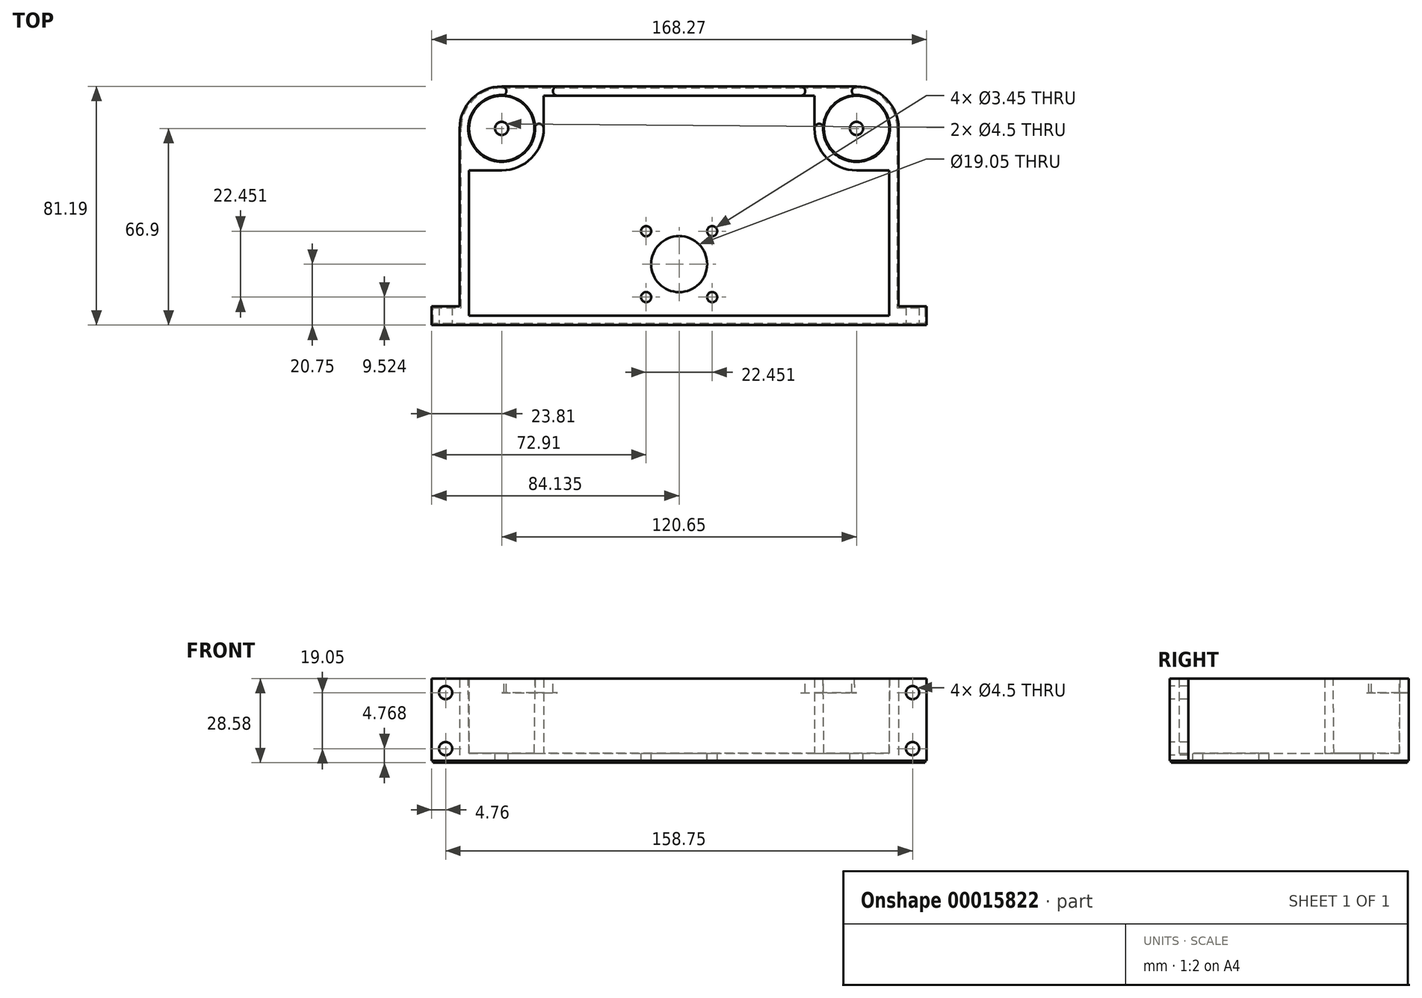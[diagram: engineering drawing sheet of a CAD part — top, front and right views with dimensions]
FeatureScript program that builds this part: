
annotation { "Feature Type Name" : "Feature", "Feature Type Description" : "" }
export const myFeature = defineFeature(function(context is Context, id is Id, definition is map)
    precondition{}
    {
        {
            var Q0;
            Q0=qCreatedBy(makeId("Top.planeOp"),FACE);
            var sketch = newSketch(context, id + "F0", { "sketchPlane" : qUnion([Q0])});
            skCircle(sketch, "E0", {"center": v(0, 0) * mm, "radius": 11.11 * mm});
            skLineSegment(sketch, "E1", {"start": v(0, 0) * mm, "end": v(120.65, 0) * mm, "construction": true});
            skCircle(sketch, "E2", {"center": v(120.65, 0) * mm, "radius": 11.11 * mm});
            skArc(sketch, "E3", {"start": v(0, 14.29) * mm, "mid": v(-10.1, 10.1) * mm, "end": v(-14.29, 0) * mm});
            skArc(sketch, "E4", {"start": v(134.94, 0) * mm, "mid": v(130.75, 10.1) * mm, "end": v(120.65, 14.29) * mm});
            skLineSegment(sketch, "E5", {"start": v(-14.29, 0) * mm, "end": v(-14.29, -60.55) * mm});
            skLineSegment(sketch, "E6", {"start": v(134.94, 0) * mm, "end": v(134.94, -60.55) * mm});
            skLineSegment(sketch, "E7", {"start": v(134.94, -60.55) * mm, "end": v(144.46, -60.55) * mm});
            skLineSegment(sketch, "E8", {"start": v(144.46, -60.55) * mm, "end": v(144.46, -66.9) * mm});
            skLineSegment(sketch, "E9", {"start": v(144.46, -66.9) * mm, "end": v(-23.81, -66.9) * mm});
            skLineSegment(sketch, "E10", {"start": v(-23.81, -66.9) * mm, "end": v(-23.81, -60.55) * mm});
            skLineSegment(sketch, "E11", {"start": v(-23.81, -60.55) * mm, "end": v(-14.29, -60.55) * mm});
            skLineSegment(sketch, "E12", {"start": v(0, 14.29) * mm, "end": v(120.65, 14.29) * mm});
            skLineSegment(sketch, "E13", {"start": v(60.33, 0) * mm, "end": v(60.33, -66.9) * mm, "construction": true});
            skSolve(sketch);
        }
        {
            var Q0;
            Q0=qSketchRegion(id+"F0",true);
            extrude(context, id + "F1", {"entities" : qUnion([Q0]), "depth" : 25.4 * mm});
        }
        {
            var Q0;
            Q0=makeQuery(id+"F1.opExtrude","CAP_FACE",FACE,{"disambiguationData":[OSD([sQuery(id+"F0.wireOp",EDGE,"E0"),sQuery(id+"F0.wireOp",EDGE,"E2"),sQuery(id+"F0.wireOp",EDGE,"vQT7KybJ-lzgk-kh55-kQ7M-RuszsokMCCUL"),sQuery(id+"F0.wireOp",EDGE,"E3"),sQuery(id+"F0.wireOp",EDGE,"E4"),sQuery(id+"F0.wireOp",EDGE,"E5"),sQuery(id+"F0.wireOp",EDGE,"E6"),sQuery(id+"F0.wireOp",EDGE,"E7"),sQuery(id+"F0.wireOp",EDGE,"E8"),sQuery(id+"F0.wireOp",EDGE,"E9"),sQuery(id+"F0.wireOp",EDGE,"E10"),sQuery(id+"F0.wireOp",EDGE,"E11")])],"isStart":false});
            shell(context, id + "F2", {"entities" : qUnion([Q0]), "thickness" : 3.17 * mm});
        }
        {
            var Q0;
            Q0=makeQuery(id+"F2.opShell","OFFSET_FACE",FACE,{"disambiguationData":[OSD([sQuery(id+"F0.wireOp",EDGE,"E0"),sQuery(id+"F0.wireOp",EDGE,"E2"),sQuery(id+"F0.wireOp",EDGE,"vQT7KybJ-lzgk-kh55-kQ7M-RuszsokMCCUL"),sQuery(id+"F0.wireOp",EDGE,"E3"),sQuery(id+"F0.wireOp",EDGE,"E4"),sQuery(id+"F0.wireOp",EDGE,"E5"),sQuery(id+"F0.wireOp",EDGE,"E6"),sQuery(id+"F0.wireOp",EDGE,"E7"),sQuery(id+"F0.wireOp",EDGE,"E8"),sQuery(id+"F0.wireOp",EDGE,"E9"),sQuery(id+"F0.wireOp",EDGE,"E10"),sQuery(id+"F0.wireOp",EDGE,"E11")])]});
            var sketch = newSketch(context, id + "F3", { "sketchPlane" : qUnion([Q0])});
            skArc(sketch, "E14", {"start": v(14.29, 0) * mm, "mid": v(12.9, 6.16) * mm, "end": v(8.98, 11.11) * mm});
            skArc(sketch, "E15", {"start": v(-11.11, -8.98) * mm, "mid": v(-6.16, -12.9) * mm, "end": v(0, -14.29) * mm});
            skLineSegment(sketch, "E16.bottom", {"start": v(-11.11, -8.98) * mm, "end": v(0, -8.98) * mm, "construction": true});
            skLineSegment(sketch, "E16.top", {"start": v(-11.11, -14.29) * mm, "end": v(0, -14.29) * mm});
            skLineSegment(sketch, "E16.left", {"start": v(-11.11, -8.98) * mm, "end": v(-11.11, -14.29) * mm});
            skLineSegment(sketch, "E16.right", {"start": v(0, -8.98) * mm, "end": v(0, -14.29) * mm, "construction": true});
            skLineSegment(sketch, "E17.bottom", {"start": v(14.29, 0) * mm, "end": v(8.98, 0) * mm, "construction": true});
            skLineSegment(sketch, "E17.top", {"start": v(14.29, 11.11) * mm, "end": v(8.98, 11.11) * mm});
            skLineSegment(sketch, "E17.left", {"start": v(14.29, 0) * mm, "end": v(14.29, 11.11) * mm});
            skLineSegment(sketch, "E17.right", {"start": v(8.98, 0) * mm, "end": v(8.98, 11.11) * mm, "construction": true});
            skArc(sketch, "E18", {"start": v(111.67, 11.11) * mm, "mid": v(107.76, 6.16) * mm, "end": v(106.36, 0) * mm});
            skArc(sketch, "E19", {"start": v(120.65, -14.29) * mm, "mid": v(126.8, -12.9) * mm, "end": v(131.76, -8.98) * mm});
            skLineSegment(sketch, "E20.bottom", {"start": v(106.36, 0) * mm, "end": v(111.67, 0) * mm, "construction": true});
            skLineSegment(sketch, "E20.top", {"start": v(106.36, 11.11) * mm, "end": v(111.67, 11.11) * mm});
            skLineSegment(sketch, "E20.left", {"start": v(106.36, 0) * mm, "end": v(106.36, 11.11) * mm});
            skLineSegment(sketch, "E20.right", {"start": v(111.67, 0) * mm, "end": v(111.67, 11.11) * mm, "construction": true});
            skLineSegment(sketch, "E21.bottom", {"start": v(120.65, -14.29) * mm, "end": v(131.76, -14.29) * mm});
            skLineSegment(sketch, "E21.top", {"start": v(120.65, -8.98) * mm, "end": v(131.76, -8.98) * mm, "construction": true});
            skLineSegment(sketch, "E21.left", {"start": v(120.65, -14.29) * mm, "end": v(120.65, -8.98) * mm, "construction": true});
            skLineSegment(sketch, "E21.right", {"start": v(131.76, -14.29) * mm, "end": v(131.76, -8.98) * mm});
            skSolve(sketch);
        }
        {
            var Q0;
            Q0=qSketchRegion(id+"F3",true);
            var Q1;
            Q1=makeQuery(id+"F1.opExtrude","CAP_FACE",FACE,{"disambiguationData":[OSD([sQuery(id+"F0.wireOp",EDGE,"E0"),sQuery(id+"F0.wireOp",EDGE,"E2"),sQuery(id+"F0.wireOp",EDGE,"vQT7KybJ-lzgk-kh55-kQ7M-RuszsokMCCUL"),sQuery(id+"F0.wireOp",EDGE,"E3"),sQuery(id+"F0.wireOp",EDGE,"E4"),sQuery(id+"F0.wireOp",EDGE,"E5"),sQuery(id+"F0.wireOp",EDGE,"E6"),sQuery(id+"F0.wireOp",EDGE,"E7"),sQuery(id+"F0.wireOp",EDGE,"E8"),sQuery(id+"F0.wireOp",EDGE,"E9"),sQuery(id+"F0.wireOp",EDGE,"E10"),sQuery(id+"F0.wireOp",EDGE,"E11")])],"isStart":false});
            extrude(context, id + "F4", {"entities" : qUnion([Q0]), "operationType" : NewBodyOperationType.ADD, "endBound" : BoundingType.UP_TO_SURFACE, "endBoundEntityFace" : qUnion([Q1]), "depth" : 25.4 * mm});
        }
        {
            var Q0;
            Q0=makeQuery(id+"F2.opShell","OFFSET_FACE",FACE,{"disambiguationData":[OSD([sQuery(id+"F0.wireOp",EDGE,"E0"),sQuery(id+"F0.wireOp",EDGE,"E2"),sQuery(id+"F0.wireOp",EDGE,"vQT7KybJ-lzgk-kh55-kQ7M-RuszsokMCCUL"),sQuery(id+"F0.wireOp",EDGE,"E3"),sQuery(id+"F0.wireOp",EDGE,"E4"),sQuery(id+"F0.wireOp",EDGE,"E5"),sQuery(id+"F0.wireOp",EDGE,"E6"),sQuery(id+"F0.wireOp",EDGE,"E7"),sQuery(id+"F0.wireOp",EDGE,"E8"),sQuery(id+"F0.wireOp",EDGE,"E9"),sQuery(id+"F0.wireOp",EDGE,"E10"),sQuery(id+"F0.wireOp",EDGE,"E11")])]});
            var Q1;
            Q1=makeQuery(id+"F1.opExtrude","CAP_FACE",FACE,{"disambiguationData":[OSD([sQuery(id+"F0.wireOp",EDGE,"E0"),sQuery(id+"F0.wireOp",EDGE,"E2"),sQuery(id+"F0.wireOp",EDGE,"vQT7KybJ-lzgk-kh55-kQ7M-RuszsokMCCUL"),sQuery(id+"F0.wireOp",EDGE,"E3"),sQuery(id+"F0.wireOp",EDGE,"E4"),sQuery(id+"F0.wireOp",EDGE,"E5"),sQuery(id+"F0.wireOp",EDGE,"E6"),sQuery(id+"F0.wireOp",EDGE,"E7"),sQuery(id+"F0.wireOp",EDGE,"E8"),sQuery(id+"F0.wireOp",EDGE,"E9"),sQuery(id+"F0.wireOp",EDGE,"E10"),sQuery(id+"F0.wireOp",EDGE,"E11")])],"isStart":true});
            extrude(context, id + "F5", {"entities" : qUnion([Q0]), "operationType" : NewBodyOperationType.REMOVE, "endBound" : BoundingType.UP_TO_SURFACE, "oppositeDirection" : true, "endBoundEntityFace" : qUnion([Q1]), "depth" : 25.4 * mm});
        }
        {
            var Q0;
            Q0=makeQuery(id+"F1.opExtrude","CAP_FACE",FACE,{"disambiguationData":[OSD([sQuery(id+"F0.wireOp",EDGE,"E0"),sQuery(id+"F0.wireOp",EDGE,"E2"),sQuery(id+"F0.wireOp",EDGE,"vQT7KybJ-lzgk-kh55-kQ7M-RuszsokMCCUL"),sQuery(id+"F0.wireOp",EDGE,"E3"),sQuery(id+"F0.wireOp",EDGE,"E4"),sQuery(id+"F0.wireOp",EDGE,"E5"),sQuery(id+"F0.wireOp",EDGE,"E6"),sQuery(id+"F0.wireOp",EDGE,"E7"),sQuery(id+"F0.wireOp",EDGE,"E8"),sQuery(id+"F0.wireOp",EDGE,"E9"),sQuery(id+"F0.wireOp",EDGE,"E10"),sQuery(id+"F0.wireOp",EDGE,"E11")])],"isStart":true});
            var sketch = newSketch(context, id + "F6", { "sketchPlane" : qUnion([Q0])});
            skCircle(sketch, "E22", {"center": v(120.65, 0) * mm, "radius": 2.25 * mm});
            skCircle(sketch, "E23", {"center": v(0, 0) * mm, "radius": 2.25 * mm});
            skLineSegment(sketch, "E24", {"start": v(120.65, 0) * mm, "end": v(0, 0) * mm, "construction": true});
            skLineSegment(sketch, "E25.bottom", {"start": v(49.1, 34.92) * mm, "end": v(71.55, 34.92) * mm, "construction": true});
            skLineSegment(sketch, "E25.top", {"start": v(49.1, 57.38) * mm, "end": v(71.55, 57.38) * mm, "construction": true});
            skLineSegment(sketch, "E25.left", {"start": v(49.1, 34.92) * mm, "end": v(49.1, 57.38) * mm, "construction": true});
            skLineSegment(sketch, "E25.right", {"start": v(71.55, 34.92) * mm, "end": v(71.55, 57.38) * mm, "construction": true});
            skPoint(sketch, "E25.middle", {"position": v(60.32, 46.15) * mm});
            skCircle(sketch, "E26", {"center": v(60.32, 46.15) * mm, "radius": 11.11 * mm, "construction": true});
            skCircle(sketch, "E27", {"center": v(49.1, 34.92) * mm, "radius": 4.76 * mm, "construction": true});
            skCircle(sketch, "E28", {"center": v(71.55, 34.92) * mm, "radius": 1.73 * mm});
            skCircle(sketch, "E29", {"center": v(49.1, 34.92) * mm, "radius": 1.73 * mm});
            skCircle(sketch, "E30", {"center": v(49.1, 57.38) * mm, "radius": 1.73 * mm});
            skCircle(sketch, "E31", {"center": v(71.55, 57.38) * mm, "radius": 1.73 * mm});
            skCircle(sketch, "E32", {"center": v(60.32, 46.15) * mm, "radius": 9.53 * mm});
            skLineSegment(sketch, "E33", {"start": v(60.32, 66.9) * mm, "end": v(60.32, 25.4) * mm, "construction": true});
            skLineSegment(sketch, "E34", {"start": v(60.33, 25.4) * mm, "end": v(60.33, 0) * mm, "construction": true});
            skSolve(sketch);
        }
        {
            var Q0;
            {var subQ13=sQuery(id+"F0.wireOp",EDGE,"E0");var subQ16=makeQuery(id+"F1.opExtrude","CAP_EDGE",EDGE,{"disambiguationData":[OSD([subQ13])],"isStart":true});Q0=makeQuery(id+"F6.imprint","IMPRINT",FACE,{"disambiguationData":[TD([[makeQuery(id+"F6.imprint","IMPRINT",EDGE,{"derivedFrom":subQ16}),1.0]])]});}
            var Q1;
            Q1=makeQuery(id+"F6.imprint","IMPRINT",FACE,{"disambiguationData":[TD([[makeQuery(id+"F6.imprint","IMPRINT",EDGE,{"derivedFrom":sQuery(id+"F6.wireOp",EDGE,"E28")}),-1.0]])]});
            var Q2;
            Q2=makeQuery(id+"F6.imprint","IMPRINT",FACE,{"disambiguationData":[TD([[makeQuery(id+"F6.imprint","IMPRINT",EDGE,{"derivedFrom":sQuery(id+"F6.wireOp",EDGE,"E23")}),-1.0]])]});
            var Q3;
            Q3=makeQuery(id+"F6.imprint","IMPRINT",FACE,{"disambiguationData":[TD([[makeQuery(id+"F6.imprint","IMPRINT",EDGE,{"derivedFrom":sQuery(id+"F6.wireOp",EDGE,"E22")}),-1.0]])]});
            extrude(context, id + "F7", {"entities" : qUnion([Q0, Q1, Q2, Q3]), "operationType" : NewBodyOperationType.ADD, "depth" : 3.17 * mm});
        }
        {
            var Q0;
            {var subQ0=sQuery(id+"F0.wireOp",EDGE,"E9");Q0=makeQuery(id+"F7.boolean.opBoolean","MERGE",FACE,{"derivedFrom":[makeQuery(id+"F1.opExtrude","SWEPT_FACE",FACE,{"disambiguationData":[OSD([subQ0])]}),makeQuery(id+"F7.opExtrude","SWEPT_FACE",FACE,{"disambiguationData":[OSD([subQ0])]})]});}
            var sketch = newSketch(context, id + "F8", { "sketchPlane" : qUnion([Q0])});
            skLineSegment(sketch, "E35.bottom", {"start": v(-19.05, 25.4) * mm, "end": v(-23.81, 25.4) * mm, "construction": true});
            skLineSegment(sketch, "E35.top", {"start": v(-19.05, 20.64) * mm, "end": v(-23.81, 20.64) * mm, "construction": true});
            skLineSegment(sketch, "E35.left", {"start": v(-19.05, 25.4) * mm, "end": v(-19.05, 20.64) * mm, "construction": true});
            skLineSegment(sketch, "E35.right", {"start": v(-23.81, 25.4) * mm, "end": v(-23.81, 20.64) * mm, "construction": true});
            skLineSegment(sketch, "E36", {"start": v(60.33, 25.4) * mm, "end": v(60.33, -3.18) * mm, "construction": true});
            skLineSegment(sketch, "E37.bottom", {"start": v(-19.05, 20.64) * mm, "end": v(139.7, 20.64) * mm, "construction": true});
            skLineSegment(sketch, "E37.top", {"start": v(-19.05, 1.59) * mm, "end": v(139.7, 1.59) * mm, "construction": true});
            skLineSegment(sketch, "E37.left", {"start": v(-19.05, 20.64) * mm, "end": v(-19.05, 1.59) * mm, "construction": true});
            skLineSegment(sketch, "E37.right", {"start": v(139.7, 20.64) * mm, "end": v(139.7, 1.59) * mm, "construction": true});
            skPoint(sketch, "E37.middle", {"position": v(60.33, 11.11) * mm});
            skCircle(sketch, "E38", {"center": v(-19.05, 20.64) * mm, "radius": 2.25 * mm});
            skCircle(sketch, "E39", {"center": v(-19.05, 1.59) * mm, "radius": 2.25 * mm});
            skCircle(sketch, "E40", {"center": v(139.7, 1.59) * mm, "radius": 2.25 * mm});
            skCircle(sketch, "E41", {"center": v(139.7, 20.64) * mm, "radius": 2.25 * mm});
            skSolve(sketch);
        }
        {
            var Q0;
            Q0=qSketchRegion(id+"F8",true);
            var Q1;
            {var subQ0=sQuery(id+"F0.wireOp",EDGE,"E7");Q1=makeQuery(id+"F7.boolean.opBoolean","MERGE",FACE,{"derivedFrom":[makeQuery(id+"F1.opExtrude","SWEPT_FACE",FACE,{"disambiguationData":[OSD([subQ0])]}),makeQuery(id+"F7.opExtrude","SWEPT_FACE",FACE,{"disambiguationData":[OSD([subQ0])]})]});}
            extrude(context, id + "F9", {"entities" : qUnion([Q0]), "operationType" : NewBodyOperationType.REMOVE, "endBound" : BoundingType.UP_TO_SURFACE, "oppositeDirection" : true, "endBoundEntityFace" : qUnion([Q1]), "depth" : 25.4 * mm});
        }
        {
            var Q0;
            Q0=makeQuery(id+"F1.opExtrude","CAP_EDGE",EDGE,{"disambiguationData":[OSD([sQuery(id+"F0.wireOp",EDGE,"E0")])],"isStart":false});
            var Q1;
            Q1=makeQuery(id+"F1.opExtrude","CAP_EDGE",EDGE,{"disambiguationData":[OSD([sQuery(id+"F0.wireOp",EDGE,"E2")])],"isStart":false});
            chamfer(context, id + "F10", {"entities" : qUnion([Q0, Q1]), "chamferType" : ChamferType.TWO_OFFSETS, "width1" : 25.4 * mm, "oppositeDirection" : false, "width2" : 0.25 * mm, "tangentPropagation" : true});
        }
        {
            var Q0;
            {var subQ0=sQuery(id+"F0.wireOp",EDGE,"E12");var subQ1=sQuery(id+"F0.wireOp",EDGE,"E11");var subQ2=sQuery(id+"F0.wireOp",EDGE,"E10");var subQ3=sQuery(id+"F0.wireOp",EDGE,"E9");var subQ4=sQuery(id+"F0.wireOp",EDGE,"E8");var subQ5=sQuery(id+"F0.wireOp",EDGE,"E7");var subQ6=sQuery(id+"F0.wireOp",EDGE,"E6");var subQ7=sQuery(id+"F0.wireOp",EDGE,"E5");var subQ8=sQuery(id+"F0.wireOp",EDGE,"E4");var subQ9=sQuery(id+"F0.wireOp",EDGE,"E3");var subQ10=sQuery(id+"F0.wireOp",EDGE,"E2");var subQ11=sQuery(id+"F0.wireOp",EDGE,"E0");Q0=makeQuery(id+"F4.boolean.opBoolean","MERGE",FACE,{"derivedFrom":[makeQuery(id+"F1.opExtrude","CAP_FACE",FACE,{"disambiguationData":[OSD([subQ11,subQ10,subQ9,subQ8,subQ7,subQ6,subQ5,subQ4,subQ3,subQ2,subQ1,subQ0])],"isStart":false}),makeQuery(id+"F4.opExtrude","CAP_FACE",FACE,{"disambiguationData":[OSD([subQ11,subQ10,subQ9,subQ8,subQ7,subQ6,subQ5,subQ4,subQ3,subQ2,subQ1,subQ0]),ownerDisambiguation([makeQuery(id+"F4.opExtrude","SWEPT_BODY",BODY,{"disambiguationData":[OSD([sQuery(id+"F3.wireOp",EDGE,"E14"),sQuery(id+"F3.wireOp",EDGE,"E17.top"),sQuery(id+"F3.wireOp",EDGE,"E17.left")])]})])],"isStart":false}),makeQuery(id+"F4.opExtrude","CAP_FACE",FACE,{"disambiguationData":[OSD([subQ11,subQ10,subQ9,subQ8,subQ7,subQ6,subQ5,subQ4,subQ3,subQ2,subQ1,subQ0]),ownerDisambiguation([makeQuery(id+"F4.opExtrude","SWEPT_BODY",BODY,{"disambiguationData":[OSD([sQuery(id+"F3.wireOp",EDGE,"E15"),sQuery(id+"F3.wireOp",EDGE,"E16.top"),sQuery(id+"F3.wireOp",EDGE,"E16.left")])]})])],"isStart":false}),makeQuery(id+"F4.opExtrude","CAP_FACE",FACE,{"disambiguationData":[OSD([subQ11,subQ10,subQ9,subQ8,subQ7,subQ6,subQ5,subQ4,subQ3,subQ2,subQ1,subQ0]),ownerDisambiguation([makeQuery(id+"F4.opExtrude","SWEPT_BODY",BODY,{"disambiguationData":[OSD([sQuery(id+"F3.wireOp",EDGE,"E18"),sQuery(id+"F3.wireOp",EDGE,"E20.top"),sQuery(id+"F3.wireOp",EDGE,"E20.left")])]})])],"isStart":false}),makeQuery(id+"F4.opExtrude","CAP_FACE",FACE,{"disambiguationData":[OSD([subQ11,subQ10,subQ9,subQ8,subQ7,subQ6,subQ5,subQ4,subQ3,subQ2,subQ1,subQ0]),ownerDisambiguation([makeQuery(id+"F4.opExtrude","SWEPT_BODY",BODY,{"disambiguationData":[OSD([sQuery(id+"F3.wireOp",EDGE,"E19"),sQuery(id+"F3.wireOp",EDGE,"E21.bottom"),sQuery(id+"F3.wireOp",EDGE,"E21.right")])]})])],"isStart":false})]});}
            var sketch = newSketch(context, id + "F11", { "sketchPlane" : qUnion([Q0])});
            skArc(sketch, "E42", {"start": v(109.54, 0) * mm, "mid": v(107.95, 1.59) * mm, "end": v(106.36, 0) * mm});
            skArc(sketch, "E43", {"start": v(120.65, 14.29) * mm, "mid": v(119.06, 12.7) * mm, "end": v(120.65, 11.11) * mm});
            skArc(sketch, "E44", {"start": v(120.65, 11.11) * mm, "mid": v(112.8, 7.86) * mm, "end": v(109.54, 0) * mm});
            skLineSegment(sketch, "E45.top", {"start": v(106.36, 11.11) * mm, "end": v(101.64, 11.11) * mm});
            skLineSegment(sketch, "E45.left", {"start": v(106.36, 0) * mm, "end": v(106.36, 11.11) * mm});
            skArc(sketch, "E46", {"start": v(101.64, 11.11) * mm, "mid": v(103.22, 12.7) * mm, "end": v(101.64, 14.29) * mm});
            skLineSegment(sketch, "E47", {"start": v(101.64, 14.29) * mm, "end": v(120.65, 14.29) * mm});
            skLineSegment(sketch, "E48", {"start": v(120.65, 0) * mm, "end": v(109.54, 0) * mm, "construction": true});
            skLineSegment(sketch, "E49", {"start": v(109.54, 0) * mm, "end": v(109.54, 13.47) * mm, "construction": true});
            skCircle(sketch, "E50", {"center": v(109.54, 13.47) * mm, "radius": 6.35 * mm, "construction": true});
            skArc(sketch, "E51", {"start": v(14.29, 0) * mm, "mid": v(12.7, 1.59) * mm, "end": v(11.11, 0) * mm});
            skArc(sketch, "E52", {"start": v(0, 11.11) * mm, "mid": v(1.59, 12.7) * mm, "end": v(0, 14.29) * mm});
            skLineSegment(sketch, "E53", {"start": v(0, 14.29) * mm, "end": v(19.01, 14.29) * mm});
            skLineSegment(sketch, "E54", {"start": v(14.29, 11.11) * mm, "end": v(19.01, 11.11) * mm});
            skLineSegment(sketch, "E55", {"start": v(14.29, 0) * mm, "end": v(14.29, 11.11) * mm});
            skArc(sketch, "E56", {"start": v(11.11, 0) * mm, "mid": v(7.86, 7.86) * mm, "end": v(0, 11.11) * mm});
            skArc(sketch, "E57", {"start": v(19.01, 14.29) * mm, "mid": v(17.43, 12.7) * mm, "end": v(19.01, 11.11) * mm});
            skSolve(sketch);
        }
        {
            var Q0;
            Q0 = qSketchRegion(id + "F11", true);
            extrude(context, id + "F12", {"entities" : qUnion([Q0]), "operationType" : NewBodyOperationType.REMOVE, "oppositeDirection" : true, "depth" : 4.76 * mm});
        }
        {
            var Q0;
            {var subQ0=sQuery(id+"F0.wireOp",EDGE,"E8");Q0=makeQuery(id+"F7.boolean.opBoolean","MERGE",FACE,{"derivedFrom":[makeQuery(id+"F1.opExtrude","SWEPT_FACE",FACE,{"disambiguationData":[OSD([subQ0])]}),makeQuery(id+"F7.opExtrude","SWEPT_FACE",FACE,{"disambiguationData":[OSD([subQ0])]})]});}
            var sketch = newSketch(context, id + "F13", { "sketchPlane" : qUnion([Q0])});
            skLineSegment(sketch, "E58.bottom", {"start": v(-66.9, -3.18) * mm, "end": v(-66.4, -3.18) * mm});
            skLineSegment(sketch, "E58.top", {"start": v(-66.9, -2.54) * mm, "end": v(-66.4, -2.54) * mm});
            skLineSegment(sketch, "E58.left", {"start": v(-66.9, -3.18) * mm, "end": v(-66.9, -2.54) * mm});
            skLineSegment(sketch, "E58.right", {"start": v(-66.4, -3.18) * mm, "end": v(-66.4, -2.54) * mm});
            skSolve(sketch);
        }
        {
            var Q0;
            Q0=makeQuery(id+"F13.imprint","IMPRINT",FACE,{"disambiguationData":[TD([[makeQuery(id+"F13.imprint","IMPRINT",EDGE,{"derivedFrom":sQuery(id+"F13.wireOp",EDGE,"E58.bottom")}),-1.0]])]});
            var Q1;
            Q1=makeQuery(id+"F7.opExtrude","CAP_EDGE",EDGE,{"disambiguationData":[OSD([sQuery(id+"F0.wireOp",EDGE,"E9")])],"isStart":false});
            var Q2;
            Q2=makeQuery(id+"F7.opExtrude","CAP_EDGE",EDGE,{"disambiguationData":[OSD([sQuery(id+"F0.wireOp",EDGE,"E10")])],"isStart":false});
            var Q3;
            Q3=makeQuery(id+"F7.opExtrude","CAP_EDGE",EDGE,{"disambiguationData":[OSD([sQuery(id+"F0.wireOp",EDGE,"E11")])],"isStart":false});
            var Q4;
            Q4=makeQuery(id+"F7.opExtrude","CAP_EDGE",EDGE,{"disambiguationData":[OSD([sQuery(id+"F0.wireOp",EDGE,"E5")])],"isStart":false});
            var Q5;
            Q5=makeQuery(id+"F7.opExtrude","CAP_EDGE",EDGE,{"disambiguationData":[OSD([sQuery(id+"F0.wireOp",EDGE,"E3")])],"isStart":false});
            var Q6;
            Q6=makeQuery(id+"F7.opExtrude","CAP_EDGE",EDGE,{"disambiguationData":[OSD([sQuery(id+"F0.wireOp",EDGE,"E12")])],"isStart":false});
            var Q7;
            Q7=makeQuery(id+"F7.opExtrude","CAP_EDGE",EDGE,{"disambiguationData":[OSD([sQuery(id+"F0.wireOp",EDGE,"E4")])],"isStart":false});
            var Q8;
            Q8=makeQuery(id+"F7.opExtrude","CAP_EDGE",EDGE,{"disambiguationData":[OSD([sQuery(id+"F0.wireOp",EDGE,"E6")])],"isStart":false});
            var Q9;
            Q9=makeQuery(id+"F7.opExtrude","CAP_EDGE",EDGE,{"disambiguationData":[OSD([sQuery(id+"F0.wireOp",EDGE,"E7")])],"isStart":false});
            var Q10;
            Q10=makeQuery(id+"F7.opExtrude","CAP_EDGE",EDGE,{"disambiguationData":[OSD([sQuery(id+"F0.wireOp",EDGE,"E8")])],"isStart":false});
            sweep(context, id + "F14", {"operationType" : NewBodyOperationType.REMOVE, "profiles" : qUnion([Q0]), "path" : qUnion([Q1, Q2, Q3, Q4, Q5, Q6, Q7, Q8, Q9, Q10])});
        }
    });
